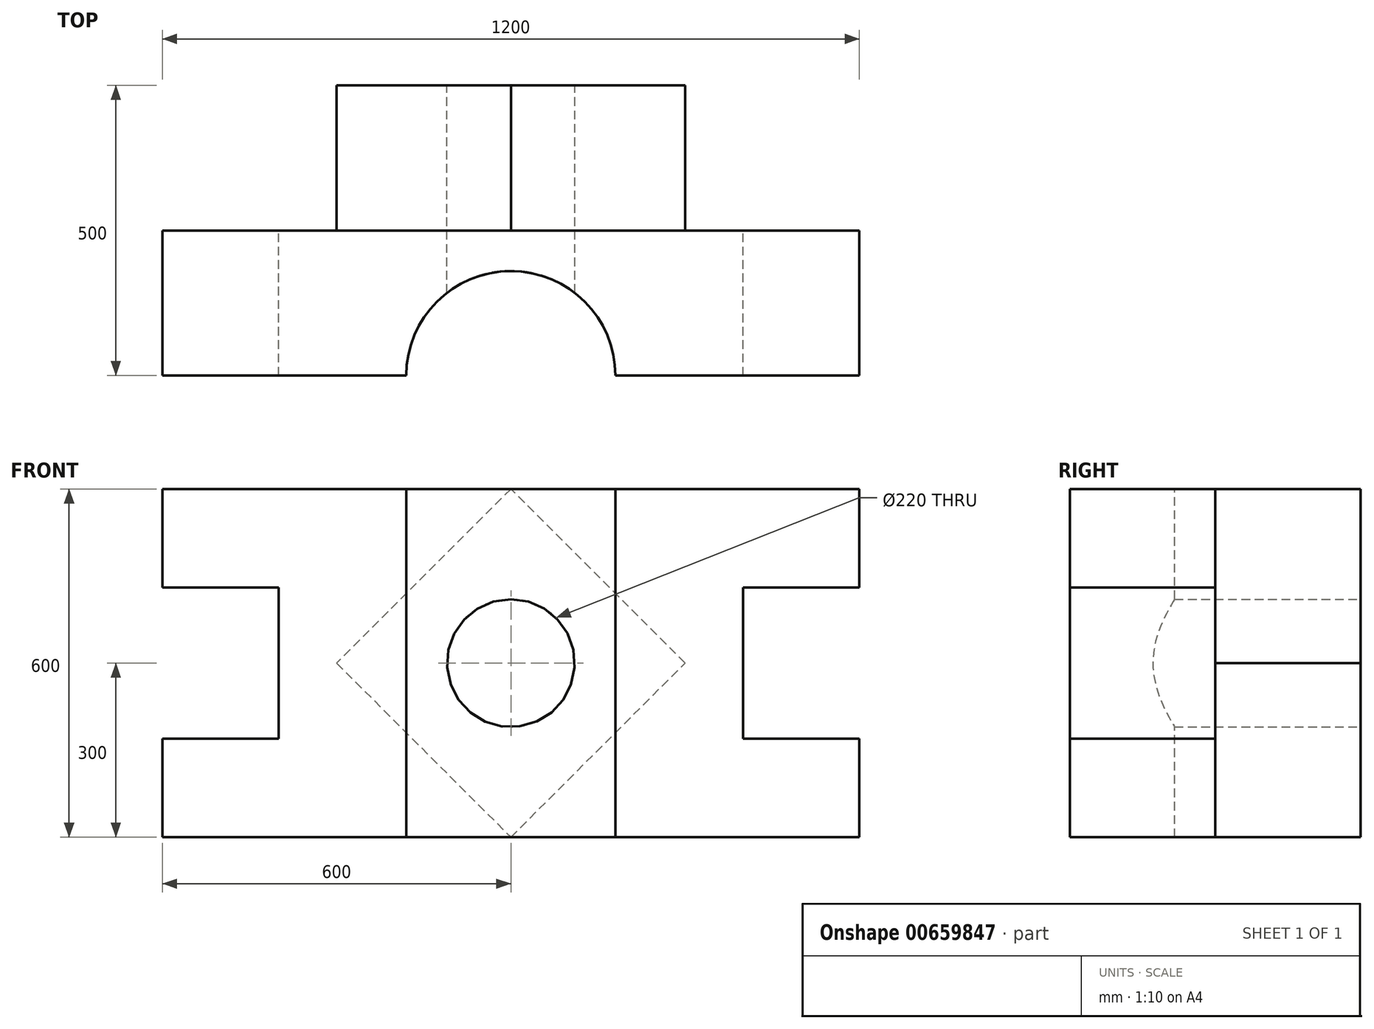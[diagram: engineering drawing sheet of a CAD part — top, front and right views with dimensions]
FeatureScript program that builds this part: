
annotation { "Feature Type Name" : "Feature", "Feature Type Description" : "" }
export const myFeature = defineFeature(function(context is Context, id is Id, definition is map)
    precondition{}
    {
        {
            var Q0;
            Q0=qCreatedBy(makeId("Front.planeOp"),FACE);
            var sketch = newSketch(context, id + "F0", { "sketchPlane" : qUnion([Q0])});
            skLineSegment(sketch, "E0.bottom", {"start": v(600, -300) * mm, "end": v(-600, -300) * mm});
            skLineSegment(sketch, "E0.top", {"start": v(600, 300) * mm, "end": v(-600, 300) * mm});
            skLineSegment(sketch, "E0.left", {"start": v(600, -300) * mm, "end": v(600, -130) * mm});
            skLineSegment(sketch, "E0.right", {"start": v(-600, -300) * mm, "end": v(-600, -130) * mm});
            skPoint(sketch, "E0.middle", {"position": v(0, 0) * mm});
            skLineSegment(sketch, "E1.bottom", {"start": v(600, -130) * mm, "end": v(400, -130) * mm});
            skLineSegment(sketch, "E1.top", {"start": v(600, 130) * mm, "end": v(400, 130) * mm});
            skLineSegment(sketch, "E1.right", {"start": v(400, -130) * mm, "end": v(400, 130) * mm});
            skPoint(sketch, "E1.middle", {"position": v(600, 0) * mm});
            skPoint(sketch, "E2.orphan", {"position": v(800, -130) * mm});
            skPoint(sketch, "E3.orphan", {"position": v(800, 130) * mm});
            skLineSegment(sketch, "E4.trimOffspring", {"start": v(600, 130) * mm, "end": v(600, 300) * mm});
            skLineSegment(sketch, "E5.bottom", {"start": v(-400, 130) * mm, "end": v(-600, 130) * mm});
            skLineSegment(sketch, "E5.top", {"start": v(-400, -130) * mm, "end": v(-600, -130) * mm});
            skLineSegment(sketch, "E5.left", {"start": v(-400, 130) * mm, "end": v(-400, -130) * mm});
            skPoint(sketch, "E5.middle", {"position": v(-600, 0) * mm});
            skPoint(sketch, "E5.right.start.orphan", {"position": v(-800, 130) * mm});
            skPoint(sketch, "E6.orphan", {"position": v(-800, -130) * mm});
            skLineSegment(sketch, "E7.trimOffspring", {"start": v(-600, 130) * mm, "end": v(-600, 300) * mm});
            skSolve(sketch);
        }
        {
            var Q0;
            Q0 = qSketchRegion(id + "F0", true);
            extrude(context, id + "F1", {"entities" : qUnion([Q0]), "depth" : 250 * mm, "offsetDistance" : 25 * mm});
        }
        {
            var Q0;
            Q0=makeQuery(id+"F1.opExtrude","SWEPT_FACE",FACE,{"disambiguationData":[OSD([sQuery(id+"F0.wireOp",EDGE,"E0.top")])]});
            var sketch = newSketch(context, id + "F2", { "sketchPlane" : qUnion([Q0])});
            skPoint(sketch, "E8.center.orphan", {"position": v(0, -250) * mm});
            skArc(sketch, "E9", {"start": v(180, -250) * mm, "mid": v(0, -70) * mm, "end": v(-180, -250) * mm});
            skLineSegment(sketch, "E10", {"start": v(-180, -250) * mm, "end": v(180, -250) * mm});
            skSolve(sketch);
        }
        {
            var Q0;
            Q0=makeQuery(id+"F2.imprint","IMPRINT",FACE,{"disambiguationData":[TD([[makeQuery(id+"F2.imprint","IMPRINT",EDGE,{"derivedFrom":sQuery(id+"F2.wireOp",EDGE,"E8")}),1.0]])]});
            var Q1;
            Q1=makeQuery(id+"F2.imprint","IMPRINT",FACE,{"disambiguationData":[TD([[makeQuery(id+"F2.imprint","IMPRINT",EDGE,{"derivedFrom":sQuery(id+"F2.wireOp",EDGE,"E9")}),1.0]])]});
            extrude(context, id + "F3", {"entities" : qUnion([Q0, Q1]), "operationType" : NewBodyOperationType.REMOVE, "endBound" : BoundingType.THROUGH_ALL, "oppositeDirection" : true, "depth" : 25 * mm, "offsetDistance" : 25 * mm});
        }
        {
            var Q0;
            Q0=makeQuery(id+"F1.opExtrude","CAP_FACE",FACE,{"disambiguationData":[OSD([sQuery(id+"F0.wireOp",EDGE,"E0.bottom"),sQuery(id+"F0.wireOp",EDGE,"E0.top"),sQuery(id+"F0.wireOp",EDGE,"E0.left"),sQuery(id+"F0.wireOp",EDGE,"E0.right"),sQuery(id+"F0.wireOp",EDGE,"E1.bottom"),sQuery(id+"F0.wireOp",EDGE,"E1.top"),sQuery(id+"F0.wireOp",EDGE,"E1.right"),sQuery(id+"F0.wireOp",EDGE,"E4.trimOffspring"),sQuery(id+"F0.wireOp",EDGE,"E5.bottom"),sQuery(id+"F0.wireOp",EDGE,"E5.top"),sQuery(id+"F0.wireOp",EDGE,"E5.left"),sQuery(id+"F0.wireOp",EDGE,"E7.trimOffspring")])],"isStart":true});
            var sketch = newSketch(context, id + "F4", { "sketchPlane" : qUnion([Q0])});
            skLineSegment(sketch, "E11", {"start": v(-300, 0) * mm, "end": v(0, 300) * mm});
            skLineSegment(sketch, "E12", {"start": v(0, 300) * mm, "end": v(300, 0) * mm});
            skLineSegment(sketch, "E13", {"start": v(300, 0) * mm, "end": v(0, -300) * mm});
            skLineSegment(sketch, "E14", {"start": v(0, -300) * mm, "end": v(-300, 0) * mm});
            skPoint(sketch, "E15.orphan", {"position": v(300, 300) * mm});
            skPoint(sketch, "E16.orphan", {"position": v(-300, 300) * mm});
            skPoint(sketch, "E17.end.orphan", {"position": v(-300, -300) * mm});
            skPoint(sketch, "E18.end.orphan", {"position": v(300, -300) * mm});
            skSolve(sketch);
        }
        {
            var Q0;
            Q0=makeQuery(id+"F4.imprint","IMPRINT",FACE,{"disambiguationData":[TD([[makeQuery(id+"F4.imprint","IMPRINT",EDGE,{"derivedFrom":sQuery(id+"F4.wireOp",EDGE,"E11")}),-1.0]])]});
            extrude(context, id + "F5", {"entities" : qUnion([Q0]), "operationType" : NewBodyOperationType.ADD, "depth" : 250 * mm, "offsetDistance" : 25 * mm});
        }
        {
            var Q0;
            Q0=makeQuery(id+"F5.opExtrude","CAP_FACE",FACE,{"disambiguationData":[OSD([sQuery(id+"F4.wireOp",EDGE,"E11"),sQuery(id+"F4.wireOp",EDGE,"E12"),sQuery(id+"F4.wireOp",EDGE,"E13"),sQuery(id+"F4.wireOp",EDGE,"E14")])],"isStart":false});
            var sketch = newSketch(context, id + "F6", { "sketchPlane" : qUnion([Q0])});
            skCircle(sketch, "E19", {"center": v(0, 0) * mm, "radius": 110 * mm});
            skSolve(sketch);
        }
        {
            var Q0;
            Q0=makeQuery(id+"F6.imprint","IMPRINT",FACE,{"disambiguationData":[TD([[makeQuery(id+"F6.imprint","IMPRINT",EDGE,{"derivedFrom":sQuery(id+"F6.wireOp",EDGE,"E19")}),1.0]])]});
            extrude(context, id + "F7", {"entities" : qUnion([Q0]), "operationType" : NewBodyOperationType.REMOVE, "endBound" : BoundingType.THROUGH_ALL, "oppositeDirection" : true, "depth" : 25 * mm, "offsetDistance" : 25 * mm});
        }
    });
